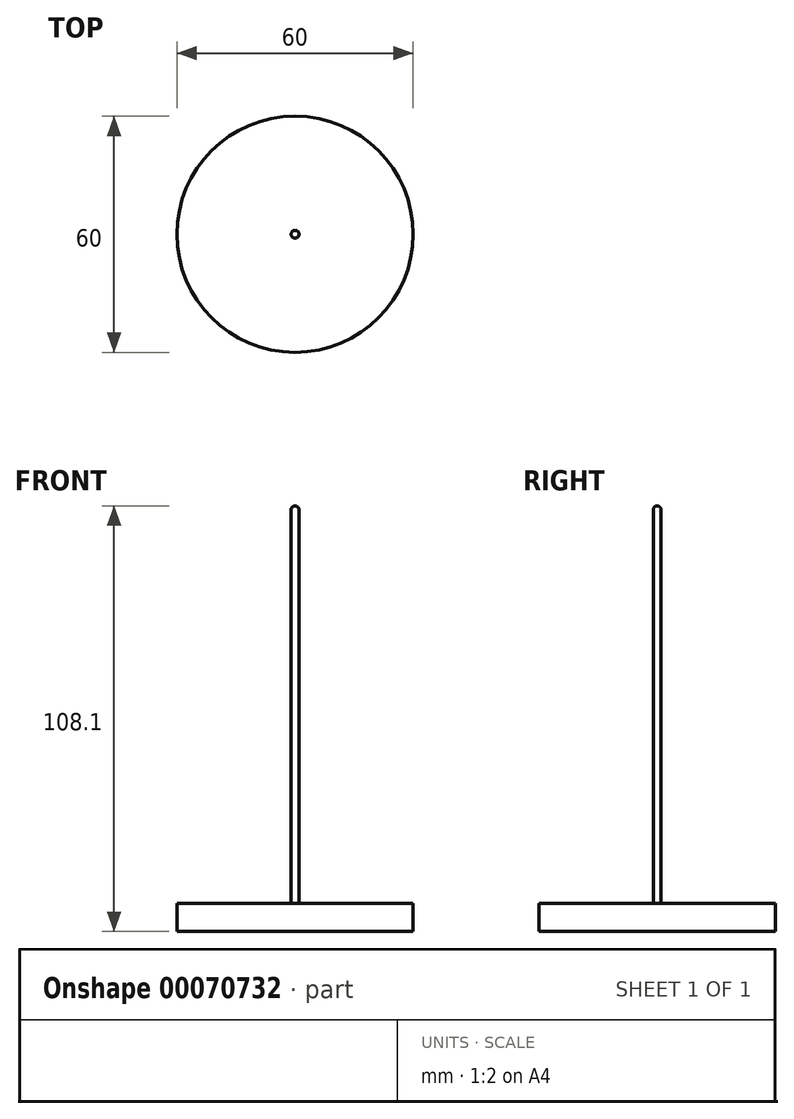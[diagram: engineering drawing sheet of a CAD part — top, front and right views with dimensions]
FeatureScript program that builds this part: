
annotation { "Feature Type Name" : "Feature", "Feature Type Description" : "" }
export const myFeature = defineFeature(function(context is Context, id is Id, definition is map)
    precondition{}
    {
        {
            var Q0;
            Q0=qCreatedBy(makeId("Front.planeOp"),FACE);
            var sketch = newSketch(context, id + "F0", { "sketchPlane" : qUnion([Q0])});
            skLineSegment(sketch, "E0", {"start": v(-1, 52.1) * mm, "end": v(-1, -47.9) * mm});
            skLineSegment(sketch, "E1", {"start": v(0, 45.3) * mm, "end": v(0, 58.73) * mm, "construction": true});
            skArc(sketch, "E2", {"start": v(0, 53.1) * mm, "mid": v(-0.7, 52.8) * mm, "end": v(-1, 52.1) * mm});
            skLineSegment(sketch, "E3.bottom", {"start": v(-1, -47.9) * mm, "end": v(-30, -47.9) * mm});
            skLineSegment(sketch, "E3.top", {"start": v(0, -55) * mm, "end": v(-30, -55) * mm});
            skLineSegment(sketch, "E3.right", {"start": v(-30, -47.9) * mm, "end": v(-30, -55) * mm});
            skLineSegment(sketch, "E4", {"start": v(0, 53.1) * mm, "end": v(0, -55) * mm});
            skSolve(sketch);
        }
        {
            var Q0;
            Q0 = qSketchRegion(id + "F0", true);
            var Q1;
            Q1=sQuery(id+"F0.wireOp",EDGE,"E4");
            revolve(context, id + "F1", {"entities" : qUnion([Q0]), "axis" : qUnion([Q1]), "revolveType" : RevolveType.FULL});
        }
    });
